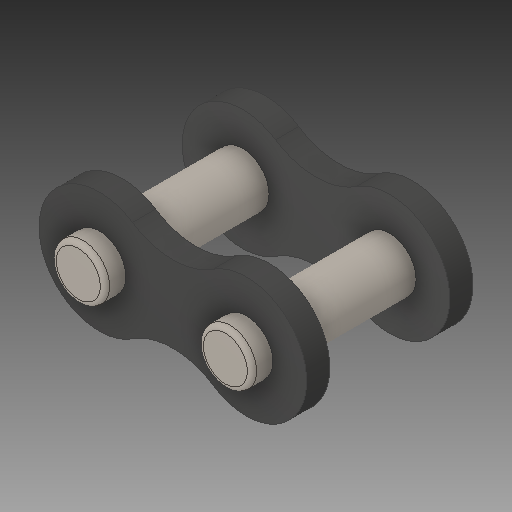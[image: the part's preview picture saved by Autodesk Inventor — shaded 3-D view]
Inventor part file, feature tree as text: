
AUTODESK INVENTOR PART (.ipt)
format: ipt  version: 2018 (Build 220112000, 112)  size: 187,904 bytes
history: native  units: in
note: dims shown in document units (in); Inventor stores cm internally (conversion verified against a paired STEP export)
features: fillet x2, other x2
ambient origin geometry x8: Origin, YZ Plane, XZ Plane, XY Plane, X Axis, Y Axis, Z Axis, Center Point
bodies: Solid1 (feature_tree), Solid2 (feature_tree), Solid3 (feature_tree), Solid4 (feature_tree)
feature tree (4):
  fillet  "Fillet2"  [1 undecoded]
  fillet  "Fillet1"  [1 undecoded]
  other  "Cut-Extrude6[1]"
  other  "Cut-Extrude6[2]"
note: 2 required parameter values undecoded (feature->parameter linkage not recoverable at this tier; creation-order binding heuristic only, values carry confidence <= 0.55)
